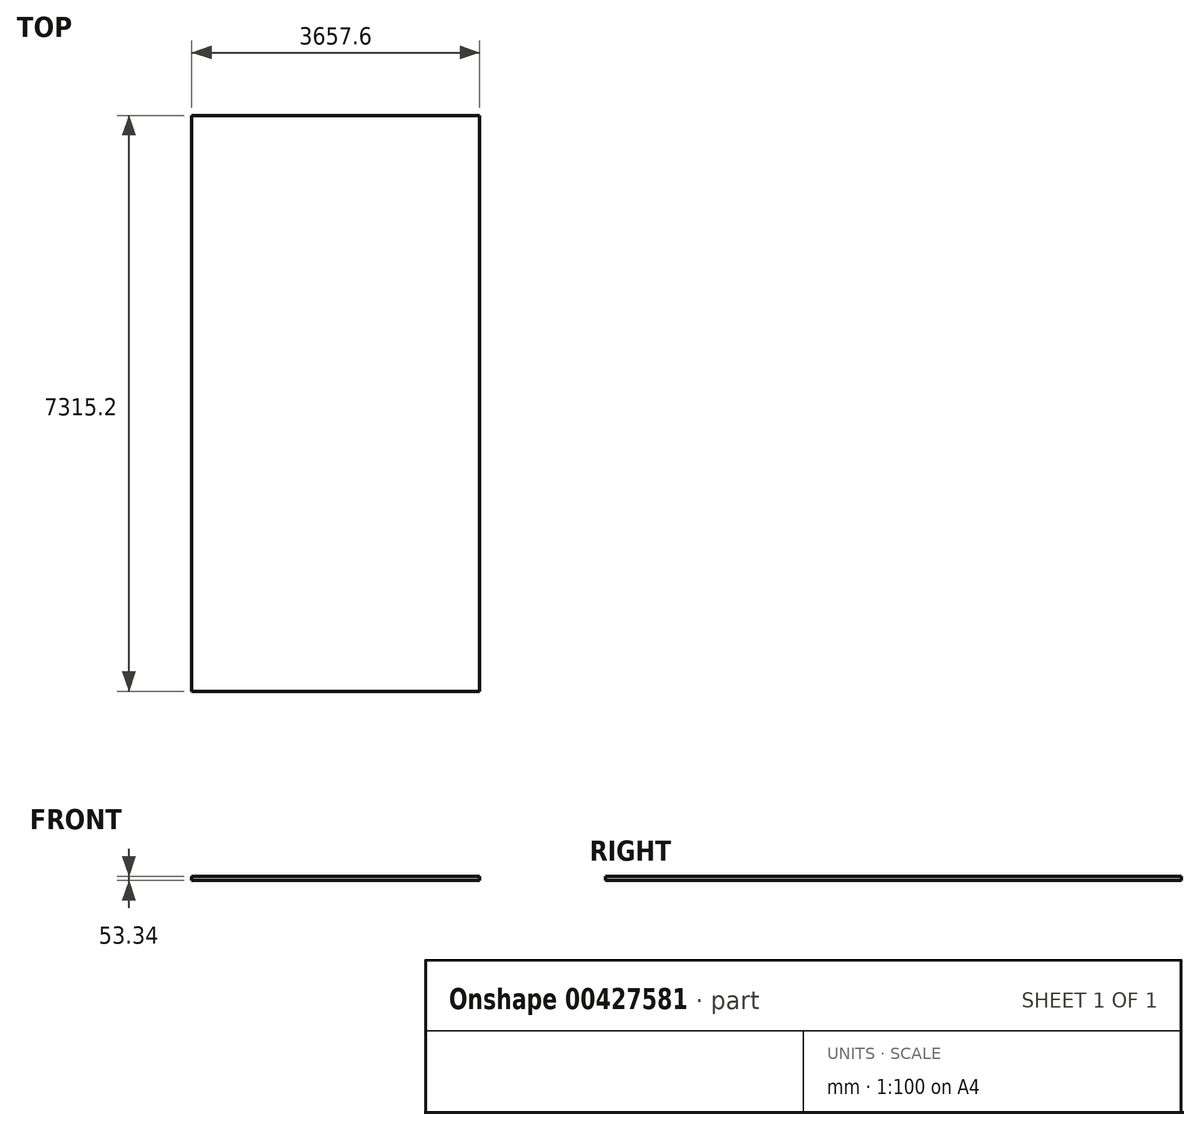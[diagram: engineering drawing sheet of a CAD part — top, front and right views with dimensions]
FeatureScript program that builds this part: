
annotation { "Feature Type Name" : "Feature", "Feature Type Description" : "" }
export const myFeature = defineFeature(function(context is Context, id is Id, definition is map)
    precondition{}
    {
        {
            var Q0;
            Q0=qCreatedBy(makeId("Top.planeOp"),FACE);
            var sketch = newSketch(context, id + "F0", { "sketchPlane" : qUnion([Q0])});
            skLineSegment(sketch, "E0.bottom", {"start": v(1828.8, -3657.6) * mm, "end": v(-1828.8, -3657.6) * mm});
            skLineSegment(sketch, "E0.top", {"start": v(1828.8, 3657.6) * mm, "end": v(-1828.8, 3657.6) * mm});
            skLineSegment(sketch, "E0.left", {"start": v(1828.8, -3657.6) * mm, "end": v(1828.8, 3657.6) * mm});
            skLineSegment(sketch, "E0.right", {"start": v(-1828.8, -3657.6) * mm, "end": v(-1828.8, 3657.6) * mm});
            skPoint(sketch, "E0.middle", {"position": v(0, 0) * mm});
            skSolve(sketch);
        }
        {
            var Q0;
            Q0=makeQuery(id+"F0.imprint","IMPRINT",FACE,{"disambiguationData":[TD([[makeQuery(id+"F0.imprint","IMPRINT",EDGE,{"derivedFrom":sQuery(id+"F0.wireOp",EDGE,"E0.bottom")}),-1.0]])]});
            extrude(context, id + "F1", {"entities" : qUnion([Q0]), "depth" : 53.34 * mm});
        }
    });
